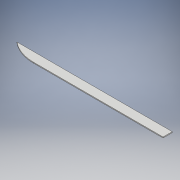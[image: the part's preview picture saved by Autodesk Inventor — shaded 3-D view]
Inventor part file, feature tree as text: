
AUTODESK INVENTOR PART (.ipt)
format: ipt  version: 2018 (Build 220112000, 112)  size: 93,184 bytes
history: native  units: mm
features: extrude x1, sketch x1, projected_geometry x1
ambient origin geometry x8: Origin, YZ Plane, XZ Plane, XY Plane, X Axis, Y Axis, Z Axis, Center Point
bodies: Body1 (feature_tree)
feature tree (3):
  extrude  "押し出し1"  Depth=3.0mm TaperAngle=0.0deg
  sketch  "スケッチ1"
  projected_geometry  "投影ループ1"
